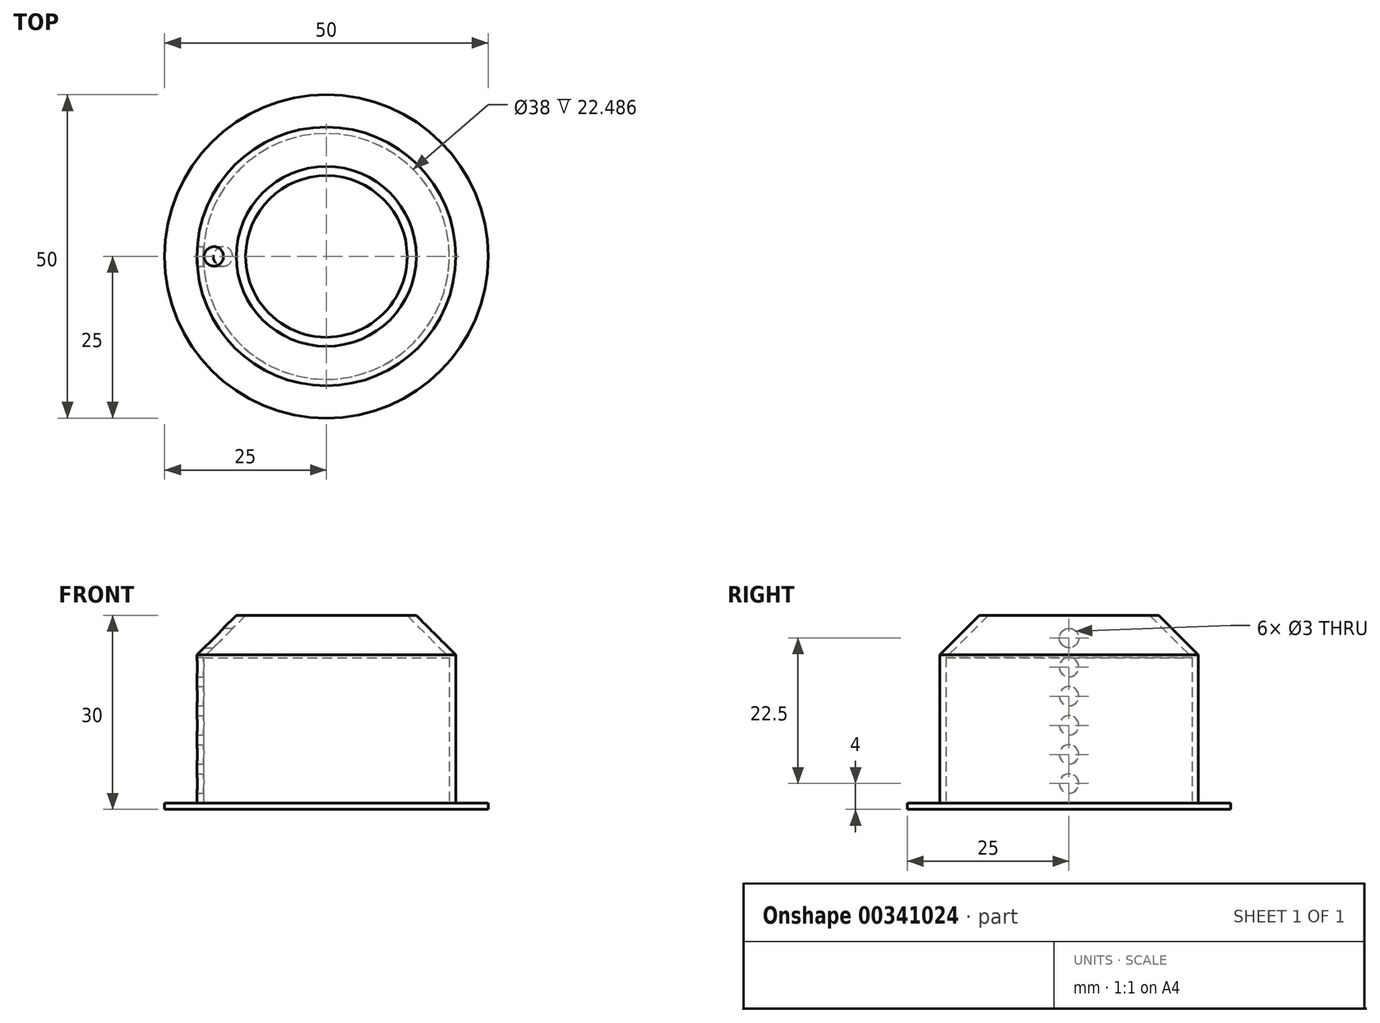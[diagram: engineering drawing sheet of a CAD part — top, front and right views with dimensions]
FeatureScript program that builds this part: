
annotation { "Feature Type Name" : "Feature", "Feature Type Description" : "" }
export const myFeature = defineFeature(function(context is Context, id is Id, definition is map)
    precondition{}
    {
        {
            var Q0;
            Q0=qCreatedBy(makeId("Top.planeOp"),FACE);
            var sketch = newSketch(context, id + "F0", { "sketchPlane" : qUnion([Q0])});
            skCircle(sketch, "E0", {"center": v(0, 0) * mm, "radius": 20 * mm});
            skSolve(sketch);
        }
        {
            var Q0;
            Q0 = qSketchRegion(id + "F0", true);
            extrude(context, id + "F1", {"entities" : qUnion([Q0]), "depth" : 30 * mm});
        }
        {
            var Q0;
            Q0=makeQuery(id+"F1.opExtrude","CAP_EDGE",EDGE,{"disambiguationData":[OSD([sQuery(id+"F0.wireOp",EDGE,"E0")])],"isStart":false});
            chamfer(context, id + "F2", {"entities" : qUnion([Q0]), "width" : 6.1 * mm, "tangentPropagation" : true});
        }
        {
            var Q0;
            Q0=qCreatedBy(makeId("Top.planeOp"),FACE);
            var sketch = newSketch(context, id + "F3", { "sketchPlane" : qUnion([Q0])});
            skCircle(sketch, "E1", {"center": v(0, 0) * mm, "radius": 25 * mm});
            skSolve(sketch);
        }
        {
            var Q0;
            Q0 = qSketchRegion(id + "F3", true);
            extrude(context, id + "F4", {"entities" : qUnion([Q0]), "operationType" : NewBodyOperationType.ADD, "depth" : 1 * mm});
        }
        {
            var Q0;
            Q0=makeQuery(id+"F1.opExtrude","CAP_FACE",FACE,{"disambiguationData":[OSD([sQuery(id+"F0.wireOp",EDGE,"E0")])],"isStart":false});
            shell(context, id + "F5", {"entities" : qUnion([Q0]), "thickness" : 1 * mm});
        }
        {
            var Q0;
            Q0=qCreatedBy(makeId("Right.planeOp"),FACE);
            var sketch = newSketch(context, id + "F6", { "sketchPlane" : qUnion([Q0])});
            skCircle(sketch, "E2", {"center": v(0, 4) * mm, "radius": 1.5 * mm});
            skLineSegment(sketch, "E3", {"start": v(0, 47.1) * mm, "end": v(0, -28.6) * mm, "construction": true});
            skCircle(sketch, "E4.0.1.0", {"center": v(0, 8.5) * mm, "radius": 1.5 * mm});
            skCircle(sketch, "E4.0.2.0", {"center": v(0, 13) * mm, "radius": 1.5 * mm});
            skCircle(sketch, "E4.0.3.0", {"center": v(0, 17.5) * mm, "radius": 1.5 * mm});
            skCircle(sketch, "E4.0.4.0", {"center": v(0, 22) * mm, "radius": 1.5 * mm});
            skCircle(sketch, "E4.0.5.0", {"center": v(0, 26.5) * mm, "radius": 1.5 * mm});
            skLineSegment(sketch, "E4.direction1", {"start": v(0, 6) * mm, "end": v(25, 6) * mm, "construction": true});
            skLineSegment(sketch, "E4.direction2", {"start": v(0, 6) * mm, "end": v(0, 10.5) * mm, "construction": true});
            skSolve(sketch);
        }
        {
            var Q0;
            Q0 = qSketchRegion(id + "F6", true);
            extrude(context, id + "F7", {"entities" : qUnion([Q0]), "operationType" : NewBodyOperationType.REMOVE, "oppositeDirection" : true, "depth" : 40 * mm});
        }
    });
